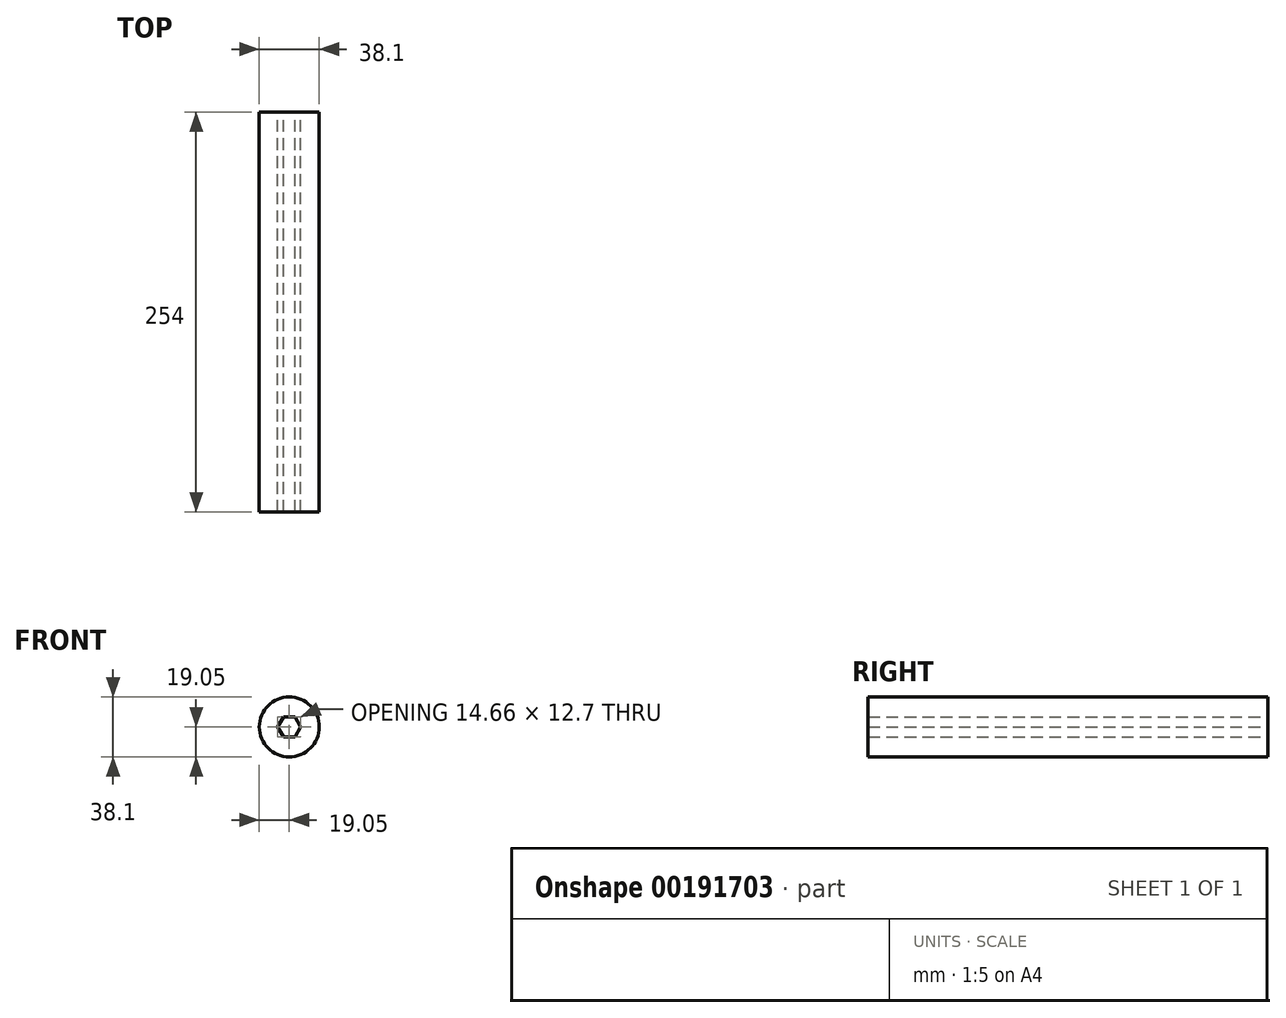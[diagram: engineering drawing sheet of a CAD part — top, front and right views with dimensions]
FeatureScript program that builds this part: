
annotation { "Feature Type Name" : "Feature", "Feature Type Description" : "" }
export const myFeature = defineFeature(function(context is Context, id is Id, definition is map)
    precondition{}
    {
        {
            var Q0;
            Q0=qCreatedBy(makeId("Front.planeOp"),FACE);
            var sketch = newSketch(context, id + "F0", { "sketchPlane" : qUnion([Q0])});
            skCircle(sketch, "E0", {"center": v(0, 0) * mm, "radius": 19.05 * mm});
            skSolve(sketch);
        }
        {
            var Q0;
            Q0 = qSketchRegion(id + "F0", true);
            extrude(context, id + "F1", {"entities" : qUnion([Q0]), "depth" : 254 * mm});
        }
        {
            var Q0;
            Q0=qCreatedBy(makeId("Front.planeOp"),FACE);
            var sketch = newSketch(context, id + "F2", { "sketchPlane" : qUnion([Q0])});
            skCircle(sketch, "E1.cCircle", {"center": v(0, 0) * mm, "radius": 7.33 * mm, "construction": true});
            skLineSegment(sketch, "E1.0", {"start": v(-7.33, 0) * mm, "end": v(-3.67, 6.35) * mm});
            skLineSegment(sketch, "E1.1", {"start": v(-3.67, 6.35) * mm, "end": v(3.67, 6.35) * mm});
            skLineSegment(sketch, "E1.2", {"start": v(3.67, 6.35) * mm, "end": v(7.33, 0) * mm});
            skLineSegment(sketch, "E1.3", {"start": v(7.33, 0) * mm, "end": v(3.67, -6.35) * mm});
            skLineSegment(sketch, "E1.4", {"start": v(3.67, -6.35) * mm, "end": v(-3.67, -6.35) * mm});
            skLineSegment(sketch, "E1.5", {"start": v(-3.67, -6.35) * mm, "end": v(-7.33, 0) * mm});
            skSolve(sketch);
        }
        {
            var Q0;
            Q0=makeQuery(id+"F2.imprint","IMPRINT",FACE,{"disambiguationData":[TD([[makeQuery(id+"F2.imprint","IMPRINT",EDGE,{"derivedFrom":sQuery(id+"F2.wireOp",EDGE,"E1.0")}),-1.0]])]});
            extrude(context, id + "F3", {"entities" : qUnion([Q0]), "operationType" : NewBodyOperationType.REMOVE, "endBound" : BoundingType.THROUGH_ALL, "depth" : 25.4 * mm});
        }
    });
